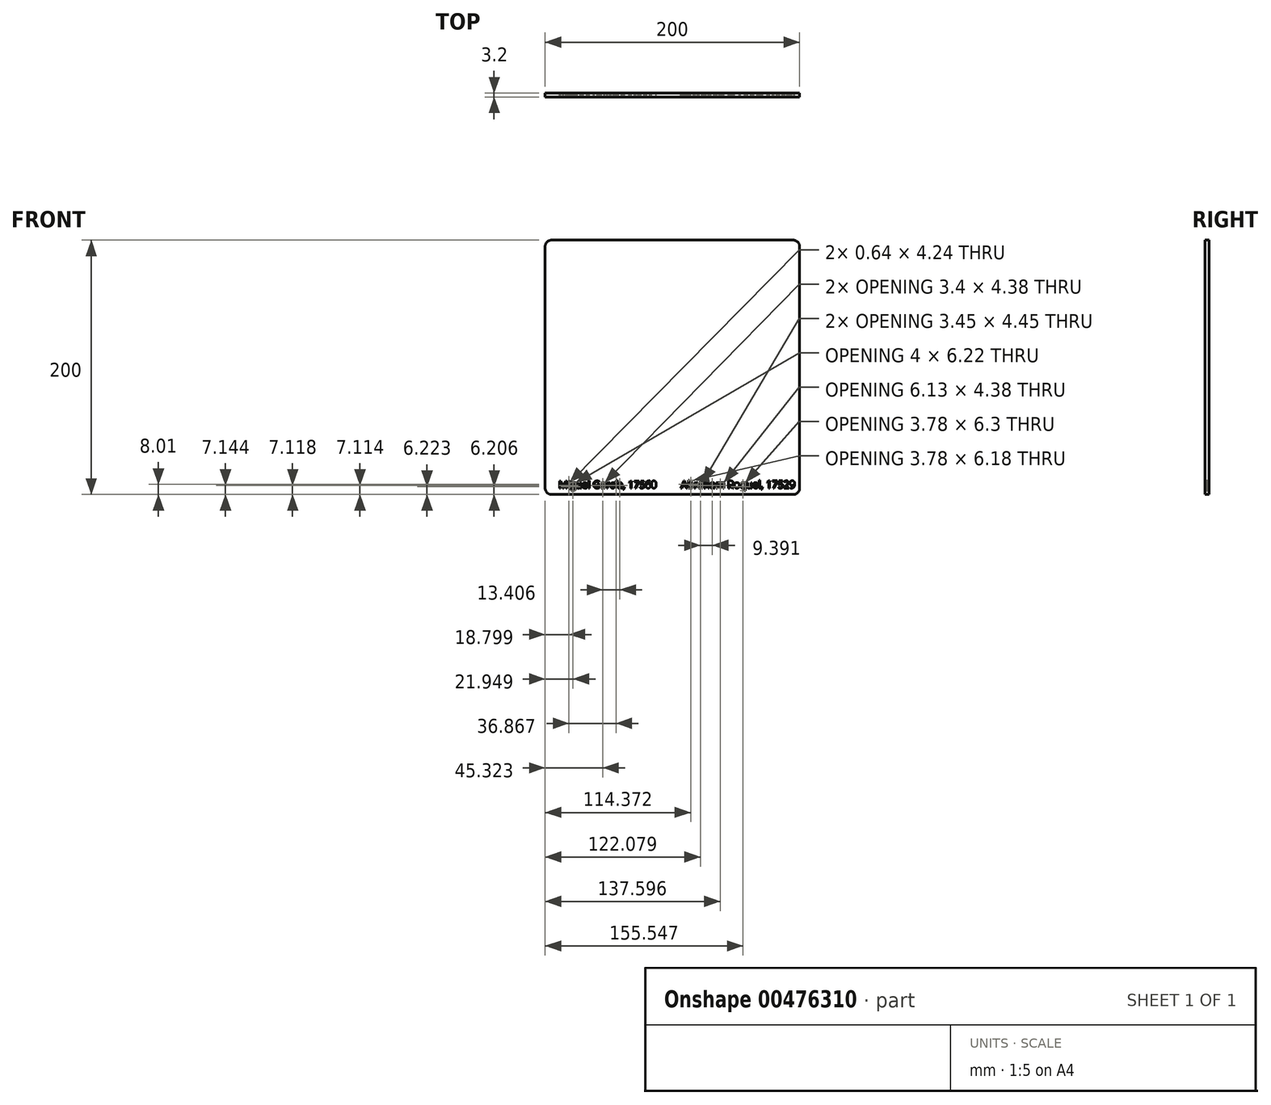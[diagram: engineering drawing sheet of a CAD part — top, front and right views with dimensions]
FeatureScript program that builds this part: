
annotation { "Feature Type Name" : "Feature", "Feature Type Description" : "" }
export const myFeature = defineFeature(function(context is Context, id is Id, definition is map)
    precondition{}
    {
        {
            var Q0;
            Q0=qCreatedBy(makeId("Front.planeOp"),FACE);
            var sketch = newSketch(context, id + "F0", { "sketchPlane" : qUnion([Q0])});
            skLineSegment(sketch, "E0.bottom", {"start": v(95, 100) * mm, "end": v(-95, 100) * mm});
            skLineSegment(sketch, "E0.top", {"start": v(95, -100) * mm, "end": v(-95, -100) * mm});
            skLineSegment(sketch, "E0.left", {"start": v(100, 95) * mm, "end": v(100, -95) * mm});
            skLineSegment(sketch, "E0.right", {"start": v(-100, 95) * mm, "end": v(-100, -95) * mm});
            skPoint(sketch, "E0.middle", {"position": v(0, 0) * mm});
            skPoint(sketch, "E1.visualSharp", {"position": v(-100, 100) * mm});
            skArc(sketch, "E1.filletArc", {"start": v(-95, 100) * mm, "mid": v(-98.54, 98.54) * mm, "end": v(-100, 95) * mm});
            skPoint(sketch, "E2.visualSharp", {"position": v(100, 100) * mm});
            skArc(sketch, "E2.filletArc", {"start": v(100, 95) * mm, "mid": v(98.54, 98.54) * mm, "end": v(95, 100) * mm});
            skPoint(sketch, "E3.visualSharp", {"position": v(100, -100) * mm});
            skArc(sketch, "E3.filletArc", {"start": v(95, -100) * mm, "mid": v(98.54, -98.54) * mm, "end": v(100, -95) * mm});
            skPoint(sketch, "E4.visualSharp", {"position": v(-100, -100) * mm});
            skArc(sketch, "E4.filletArc", {"start": v(-100, -95) * mm, "mid": v(-98.54, -98.54) * mm, "end": v(-95, -100) * mm});
            skText(sketch, "E5", { "text": "Miguel García, 17560", "fontName": "OpenSans-Regular.ttf"});
            skText(sketch, "E6", { "text": "Abraham Roquel, 17529", "fontName": "OpenSans-Regular.ttf"});
            const initialGuessF0  = {"E5": [-0.08935, -0.095, 1, 0, 0.0057], "E6": [0.00671, -0.095, 1, 0, 0.00578]};
            skSetInitialGuess(sketch, initialGuessF0);
            skSolve(sketch);
        }
        {
            var Q0;
            Q0 = qSketchRegion(id + "F0", true);
            extrude(context, id + "F1", {"entities" : qUnion([Q0]), "depth" : 3.2 * mm});
        }
    });
